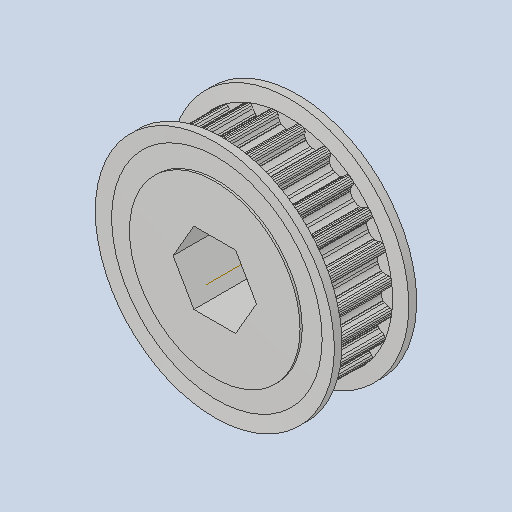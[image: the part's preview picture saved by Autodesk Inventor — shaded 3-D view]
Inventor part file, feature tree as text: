
AUTODESK INVENTOR PART (.ipt)
format: ipt  version: 2022.3 (Build 263350000, 350)  size: 667,648 bytes
history: native  units: in
note: dims shown in document units (in); Inventor stores cm internally (conversion verified against a paired STEP export)
features: mirror x1
ambient origin geometry x8: Origin, YZ Plane, XZ Plane, XY Plane, X Axis, Y Axis, Z Axis, Center Point
bodies: Solid1 (feature_tree)
feature tree (1):
  mirror  "Mirror1"
